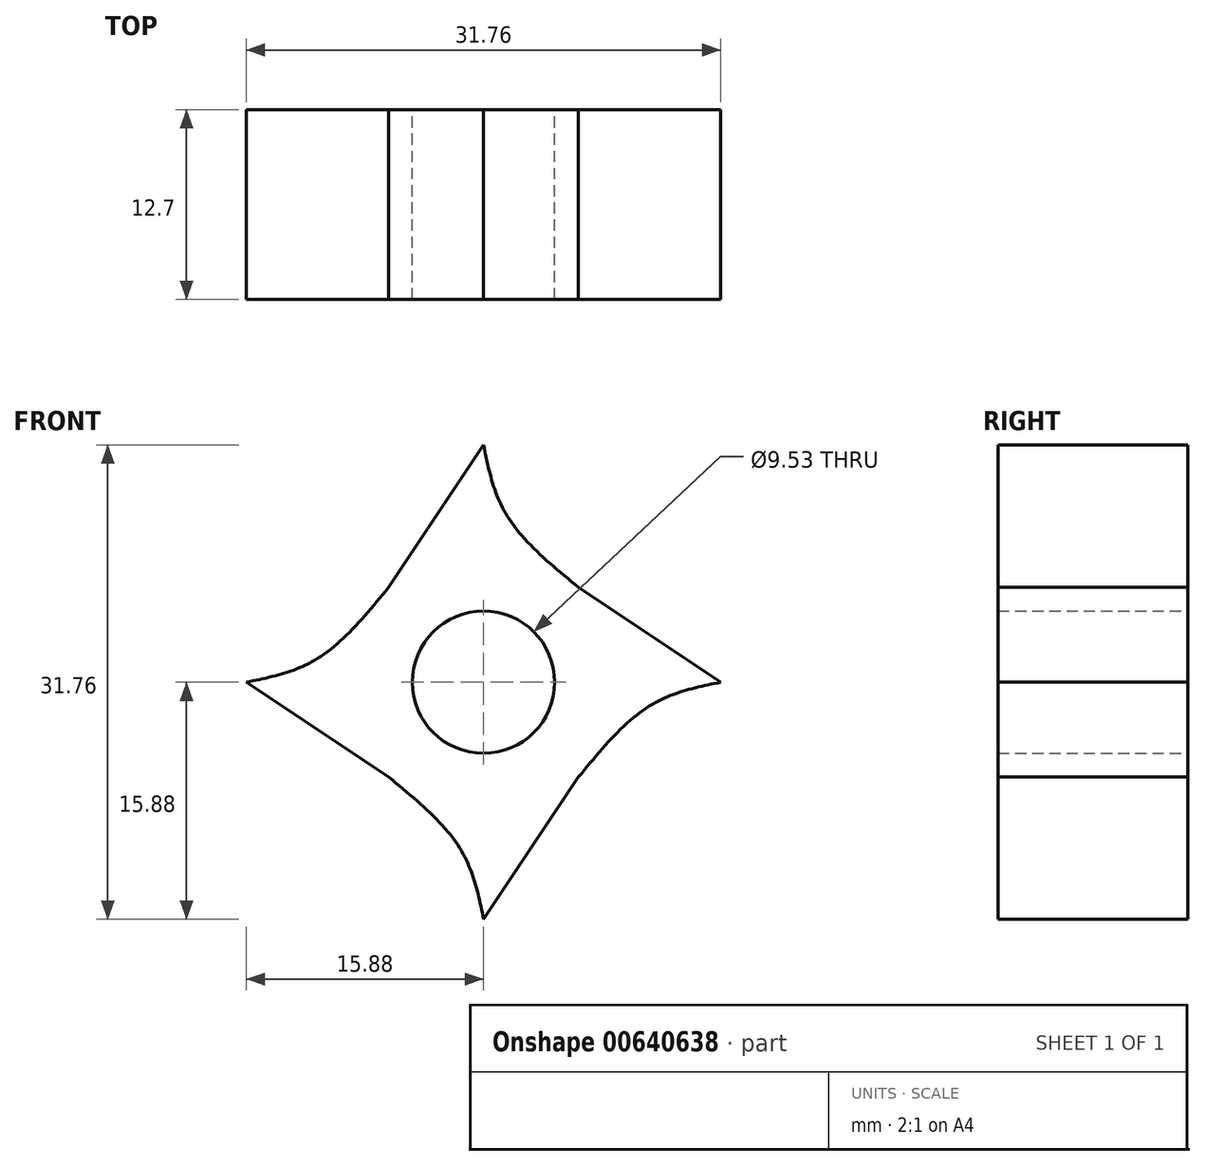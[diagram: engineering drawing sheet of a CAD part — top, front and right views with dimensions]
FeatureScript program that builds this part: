
annotation { "Feature Type Name" : "Feature", "Feature Type Description" : "" }
export const myFeature = defineFeature(function(context is Context, id is Id, definition is map)
    precondition{}
    {
        {
            var Q0;
            Q0=qCreatedBy(makeId("Front.planeOp"),FACE);
            var sketch = newSketch(context, id + "F0", { "sketchPlane" : qUnion([Q0])});
            skLineSegment(sketch, "E0.bottom", {"start": v(0, 0) * mm, "end": v(12.7, 0) * mm});
            skLineSegment(sketch, "E0.top", {"start": v(0, 12.7) * mm, "end": v(12.7, 12.7) * mm});
            skLineSegment(sketch, "E0.left", {"start": v(0, 0) * mm, "end": v(0, 12.7) * mm});
            skLineSegment(sketch, "E0.right", {"start": v(12.7, 0) * mm, "end": v(12.7, 12.7) * mm});
            skLineSegment(sketch, "E1", {"start": v(0, 6.35) * mm, "end": v(12.7, 6.35) * mm});
            skLineSegment(sketch, "E2", {"start": v(6.35, 12.7) * mm, "end": v(6.35, 0) * mm});
            skCircle(sketch, "E3", {"center": v(6.35, 6.35) * mm, "radius": 4.76 * mm});
            skLineSegment(sketch, "E4", {"start": v(6.35, 12.7) * mm, "end": v(12.7, 12.7) * mm});
            skLineSegment(sketch, "E5", {"start": v(6.35, 12.7) * mm, "end": v(6.35, 22.23) * mm});
            skLineSegment(sketch, "E6", {"start": v(0, 12.7) * mm, "end": v(6.35, 12.7) * mm});
            skLineSegment(sketch, "E7", {"start": v(6.35, 17.46) * mm, "end": v(6.35, 12.7) * mm});
            skLineSegment(sketch, "E8", {"start": v(3.17, 12.7) * mm, "end": v(6.35, 12.7) * mm});
            skLineSegment(sketch, "E9", {"start": v(9.52, 12.7) * mm, "end": v(6.35, 12.7) * mm});
            skLineSegment(sketch, "E10", {"start": v(6.35, 17.46) * mm, "end": v(7.94, 17.46) * mm});
            skPoint(sketch, "E10.endSnap0", {"position": v(7.94, 12.7) * mm});
            skFitSpline(sketch, "E11", {"points": [v(6.35, 22.22) * mm, v(7.94, 17.46) * mm, v(12.7, 12.7) * mm], "startDerivative": vector(2.16, -10.6) * mm, "endDerivative": vector(10.34, -8.5) * mm});
            skLineSegment(sketch, "E12", {"start": v(0, 12.7) * mm, "end": v(6.35, 22.23) * mm});
            skLineSegment(sketch, "E13", {"start": v(12.7, 6.35) * mm, "end": v(22.23, 6.35) * mm});
            skLineSegment(sketch, "E14", {"start": v(12.7, 12.7) * mm, "end": v(22.23, 6.35) * mm});
            skLineSegment(sketch, "E15", {"start": v(12.7, 6.35) * mm, "end": v(12.7, 0) * mm});
            skLineSegment(sketch, "E16", {"start": v(12.7, 3.17) * mm, "end": v(12.7, 6.35) * mm});
            skLineSegment(sketch, "E17", {"start": v(12.7, 6.35) * mm, "end": v(17.46, 6.35) * mm});
            skLineSegment(sketch, "E18", {"start": v(17.46, 6.35) * mm, "end": v(17.46, 4.76) * mm});
            skPoint(sketch, "E18.endSnap0", {"position": v(12.7, 4.76) * mm});
            skFitSpline(sketch, "E19", {"points": [v(22.23, 6.35) * mm, v(17.46, 4.76) * mm, v(12.7, 0) * mm], "startDerivative": vector(-10.6, -2.16) * mm, "endDerivative": vector(-8.5, -10.34) * mm});
            skLineSegment(sketch, "E20", {"start": v(6.35, 0) * mm, "end": v(6.35, -9.53) * mm});
            skLineSegment(sketch, "E21", {"start": v(6.35, -9.53) * mm, "end": v(12.7, 0) * mm});
            skLineSegment(sketch, "E22", {"start": v(6.35, 0) * mm, "end": v(0, 0) * mm});
            skLineSegment(sketch, "E23", {"start": v(3.18, 0) * mm, "end": v(6.35, 0) * mm});
            skLineSegment(sketch, "E24", {"start": v(6.35, -4.76) * mm, "end": v(4.76, -4.76) * mm});
            skPoint(sketch, "E24.endSnap0", {"position": v(4.76, 0) * mm});
            skFitSpline(sketch, "E25", {"points": [v(0, 0) * mm, v(4.76, -4.76) * mm, v(6.35, -9.53) * mm], "startDerivative": vector(10.34, -8.5) * mm, "endDerivative": vector(2.16, -10.6) * mm});
            skLineSegment(sketch, "E26", {"start": v(0, 6.35) * mm, "end": v(-9.53, 6.35) * mm});
            skLineSegment(sketch, "E27", {"start": v(-9.53, 6.35) * mm, "end": v(0, 0) * mm});
            skLineSegment(sketch, "E28", {"start": v(0, 6.35) * mm, "end": v(0, 12.7) * mm});
            skLineSegment(sketch, "E29", {"start": v(0, 9.52) * mm, "end": v(0, 6.35) * mm});
            skLineSegment(sketch, "E30", {"start": v(-4.76, 6.35) * mm, "end": v(-4.76, 7.94) * mm});
            skPoint(sketch, "E30.endSnap0", {"position": v(0, 7.94) * mm});
            skFitSpline(sketch, "E31", {"points": [v(-9.53, 6.35) * mm, v(-4.76, 7.94) * mm, v(0, 12.7) * mm], "startDerivative": vector(10.6, 2.16) * mm, "endDerivative": vector(8.5, 10.34) * mm});
            skSolve(sketch);
        }
        {
            var Q0;
            Q0 = qSketchRegion(id + "F0", true);
            extrude(context, id + "F1", {"entities" : qUnion([Q0]), "depth" : 12.7 * mm, "offsetDistance" : 25.4 * mm});
        }
    });
